# Revit family: Dorn_LD_16-270_A4_p_i_t_4031207
name_source: partatom
category: Generic Models
units: mm (PartAtom-declared; Revit-internal decimal feet)

## family parameters
Always vertical = No
Can host rebar = No
Cut with Voids When Loaded = No
Part Type = Normal
Room Calculation Point = No
Round Connector Dimension = Use Diameter
Shared = No
Work Plane-Based = Yes

## types (4) — shared parameters
Default Elevation = 1219 mm

## per-type parameters (varying)
| type | Diameter | Metal | Model | Total Width |
| 20/320 A4 | 20 mm  [stored 0.0656168 ft] | Stainless Steel A4 |  | 320 mm  [stored 1.04987 ft] |
| 16/270 A4 | 16 mm  [stored 0.0524934 ft] | Stainless Steel A4 | 1 | 270 mm  [stored 0.885827 ft] |
| 16/270 Zn | 16 mm  [stored 0.0524934 ft] | Steel, Galvanized |  | 270 mm  [stored 0.885827 ft] |
| 20/320 Zn | 20 mm  [stored 0.0656168 ft] | Steel, Galvanized |  | 320 mm  [stored 1.04987 ft] |

note: [stored X ft] marks values corroborated as IEEE doubles in the binary element streams (Revit-internal decimal feet)

## geometry (parser evidence)
native form markers: Sweep x4
no freeform markers — native parametric forms only
